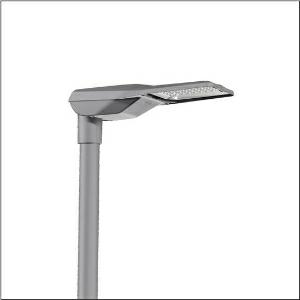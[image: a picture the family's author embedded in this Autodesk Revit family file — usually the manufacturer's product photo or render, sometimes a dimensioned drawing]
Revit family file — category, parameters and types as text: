
# Revit family: streetlight_sl_21_iq_mini___st0_8a_5xe2c41d08hb_7f29
name_source: partatom
category: Lighting Fixtures
units: mm (PartAtom-declared; Revit-internal decimal feet)

## family parameters
Cut with Voids When Loaded = No
Host = Face
Light Source = No
Part Type = Normal
Room Calculation Point = No
Round Connector Dimension = Use Diameter
Shared = No

## types (1)
- --- (1 x LED, 9860 lm, 70.9 W, 4000K)
    Apparent Load = 71 VA
    CIE Flux Codes = 38 75 97 100 100
    Color Rendering = 70
    Color Temperature = 4000K
    Default Elevation = 1800 mm
    Description = Streetlight SL 21 mini, mast luminaire, primary light control with lens, of PMMA, primary optical cover: cover, of toughened safety glass, transparent, light distribution: ST0.8a, light emission: direct distribution, primary light characteristic: asymmetric, installation type: post-top, side-entry, LED, High Power LED, rated luminous flux: 9.860lm, luminous efficacy: 139lm/W, light colour: 740, colour temperature: 4000K, control gear: ECG iQ, control: Auto-Match, Temp-Guard, Lumen-Switch, Night-Set, Smart-Wire, Light-Fading, Desk-Remote (wireless, voltage-free reading and setting of iQ features in the workshop via application-optimized NFC function/RFID function), optimised constant luminous flux control (CLO 2.0), mains connection: 220..240V, AC, 50/60Hz, start of lifetime: 71W, end of lifetime: 75W, reduction: 31W, luminaire housing, of diecast aluminium, powder-coated, Siteco® metallic grey (DB 702S), corrosivity category C5 according to DIN EN ISO 12944, length: 628mm, width: 235mm, height: 110mm, spigot size: 60/76mm (post-top) and 42/60/76mm (side-entry), mast flange for spigot size: 42mm: 5XC10008XM4, 60mm: 5XC10008XM2, 76/60mm: 5XC10108XM1, protection rating (complete): IP66, insulation class (complete): insulation class II (safety insulation), certification: CE, ENEC, VDE, impact resistance: IK09, permissible operating ambient temperature for outdoor applications: -40..+50°C, standard-compliant lighting for roads and squares, packaging unit: 1 piece

Light Distribution: ST0.8a
    Height = 110 mm
    Lamp = 1 x LED
    Lamp Light Flux = 9860 lm
    Lamp Power = 70.9 W
    Lamp count = 1
    Length = 625 mm
    Luminous efficacy = 139 lm/W
    Manufacturer = Siteco
    ModVariant = No
    Model = 5XE2C41D08HB
    Number of Poles = 1
    OnlyDefault = Yes
    Power Factor = 1
    Product Name = Streetlight SL 21 iQ mini | ST0.8a
    Product group = mast luminaire | pylon top
    ProductGroupID = 6100
    Protection Class = Protection class II
    Protection Degree = IP 66
    RLX_Detail_Level = 1
    RlxData = <blob elided: 92149 chars, md5=8ec487da>
    Socket = socket
    Standby Power = 0 W
    System Light Flux = 9860 lm
    System Power = 71 W
    Type Comments = factory setting: luminous flux: 100 % | dim-lin: 254 | 711 mA
    Type Image = l_1003519.jpg
    URL = http://relux.com
    VarID = @adj_068619
    Voltage = 0 V
    Weight = 0.00 kg
    Width = 234 mm

## geometry (parser evidence)
native form markers: Blend x4, Sweep x11
no freeform markers — native parametric forms only
